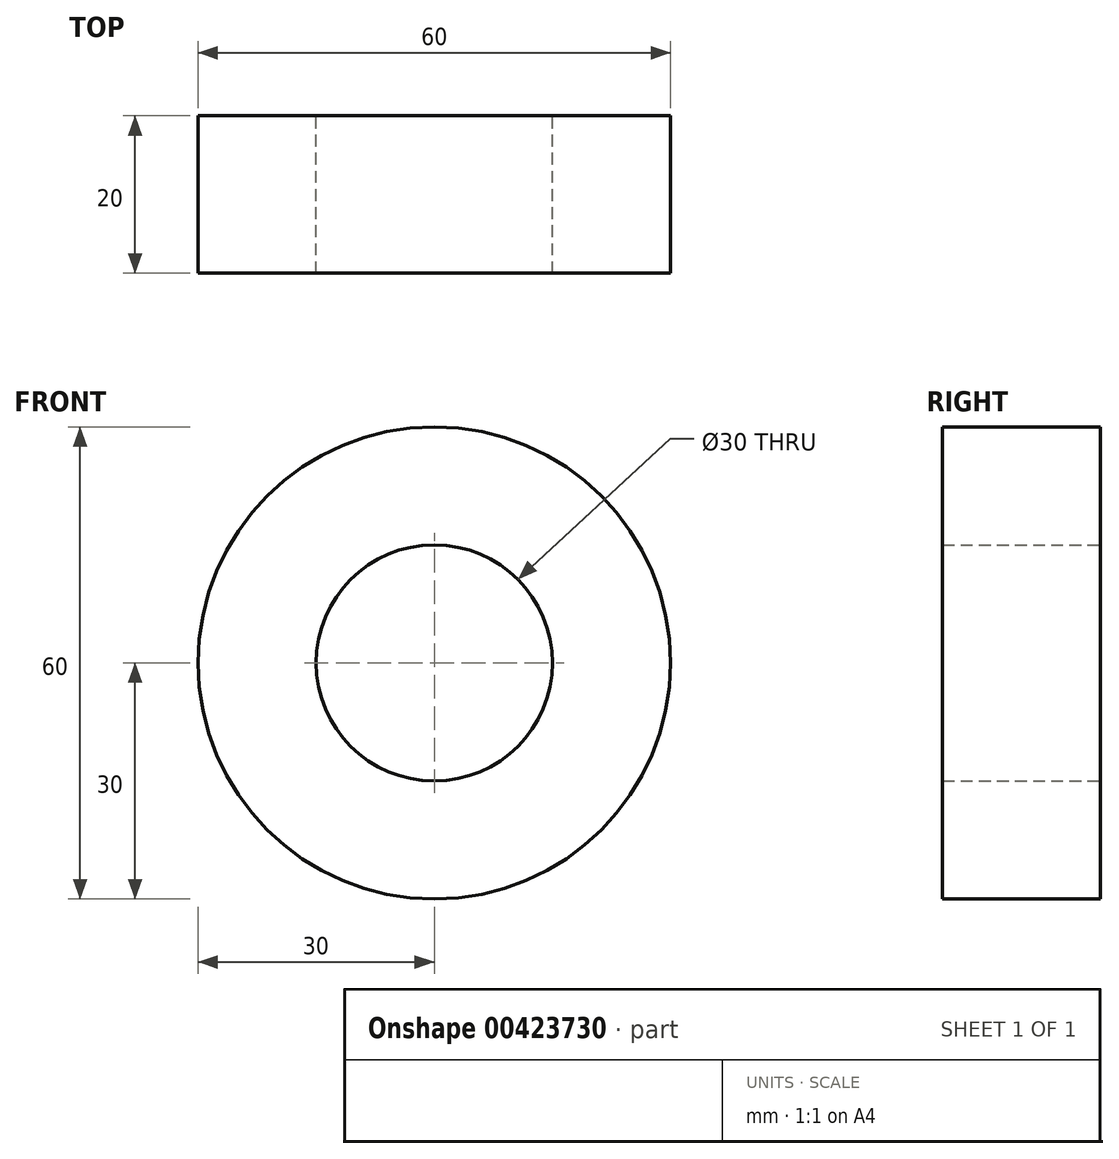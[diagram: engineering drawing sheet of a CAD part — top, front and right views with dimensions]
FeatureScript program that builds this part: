
annotation { "Feature Type Name" : "Feature", "Feature Type Description" : "" }
export const myFeature = defineFeature(function(context is Context, id is Id, definition is map)
    precondition{}
    {
        {
            var Q0;
            Q0=qCreatedBy(makeId("Front.planeOp"),FACE);
            var sketch = newSketch(context, id + "F0", { "sketchPlane" : qUnion([Q0])});
            skCircle(sketch, "E0", {"center": v(0, 0) * mm, "radius": 15 * mm});
            skCircle(sketch, "E1", {"center": v(0, 0) * mm, "radius": 30 * mm});
            skSolve(sketch);
        }
        {
            var Q0;
            Q0=makeQuery(id+"F0.imprint","IMPRINT",FACE,{"disambiguationData":[TD([[makeQuery(id+"F0.imprint","IMPRINT",EDGE,{"derivedFrom":sQuery(id+"F0.wireOp",EDGE,"E0")}),-1.0]])]});
            extrude(context, id + "F1", {"entities" : qUnion([Q0]), "endBound" : BoundingType.SYMMETRIC, "depth" : 20 * mm});
        }
    });
